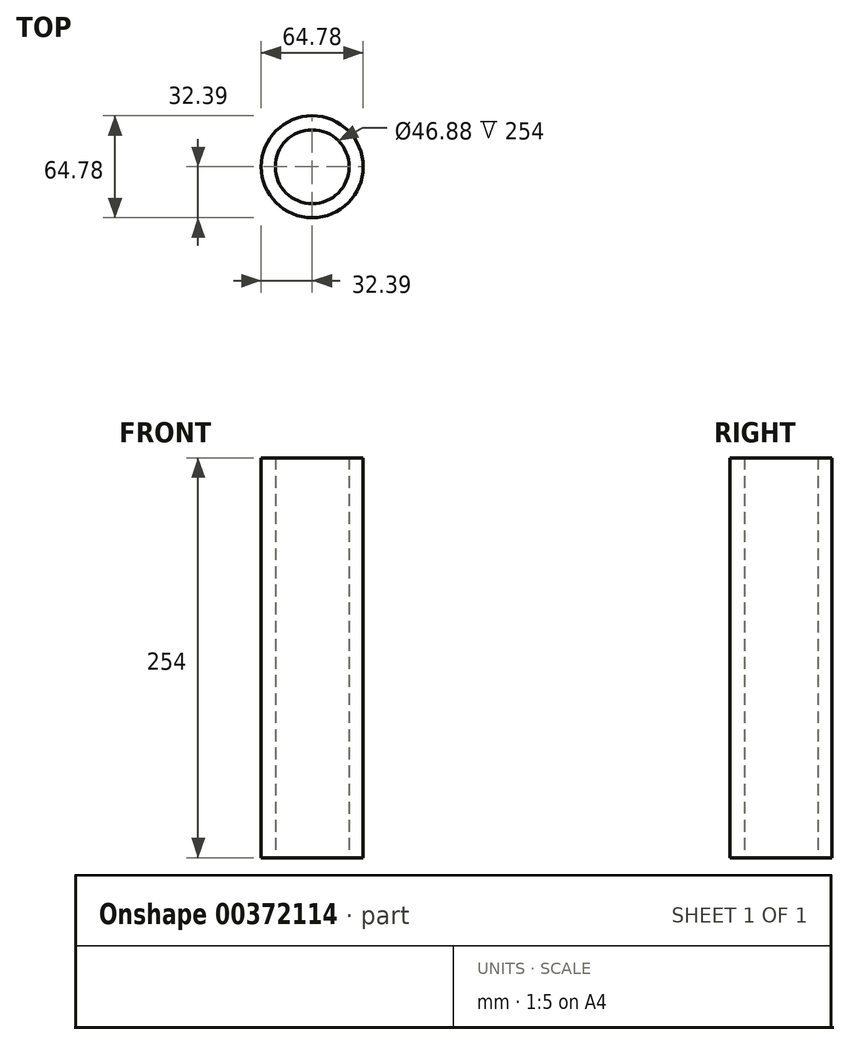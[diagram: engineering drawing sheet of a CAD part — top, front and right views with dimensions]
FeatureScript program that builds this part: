
annotation { "Feature Type Name" : "Feature", "Feature Type Description" : "" }
export const myFeature = defineFeature(function(context is Context, id is Id, definition is map)
    precondition{}
    {
        {
            var Q0;
            Q0=qCreatedBy(makeId("Top.planeOp"),FACE);
            var sketch = newSketch(context, id + "F0", { "sketchPlane" : qUnion([Q0])});
            skCircle(sketch, "E0", {"center": v(0, 0) * mm, "radius": 23.44 * mm});
            skCircle(sketch, "E1", {"center": v(0, 0) * mm, "radius": 32.39 * mm});
            skSolve(sketch);
        }
        {
            var Q0;
            Q0=makeQuery(id+"F0.imprint","IMPRINT",FACE,{"disambiguationData":[TD([[makeQuery(id+"F0.imprint","IMPRINT",EDGE,{"derivedFrom":sQuery(id+"F0.wireOp",EDGE,"E0")}),-1.0]])]});
            extrude(context, id + "F1", {"entities" : qUnion([Q0]), "depth" : 254 * mm});
        }
    });
